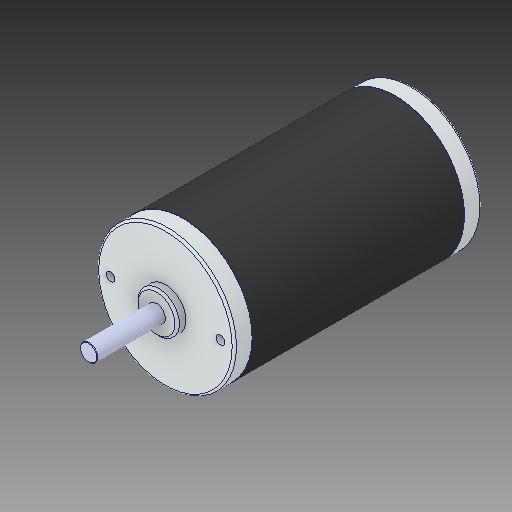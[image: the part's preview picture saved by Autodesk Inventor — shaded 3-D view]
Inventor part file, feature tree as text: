
AUTODESK INVENTOR PART (.ipt)
format: ipt  version: 2017 (Build 210142000, 142)  size: 160,768 bytes
history: native  units: in
note: dims shown in document units (in); Inventor stores cm internally (conversion verified against a paired STEP export)
features: fillet x1
ambient origin geometry x8: Origin, YZ Plane, XZ Plane, XY Plane, X Axis, Y Axis, Z Axis, Center Point
bodies: Solid1 (feature_tree)
feature tree (1):
  fillet  "Fillet4"  [1 undecoded]
note: 1 required parameter value undecoded (feature->parameter linkage not recoverable at this tier; creation-order binding heuristic only, values carry confidence <= 0.55)
